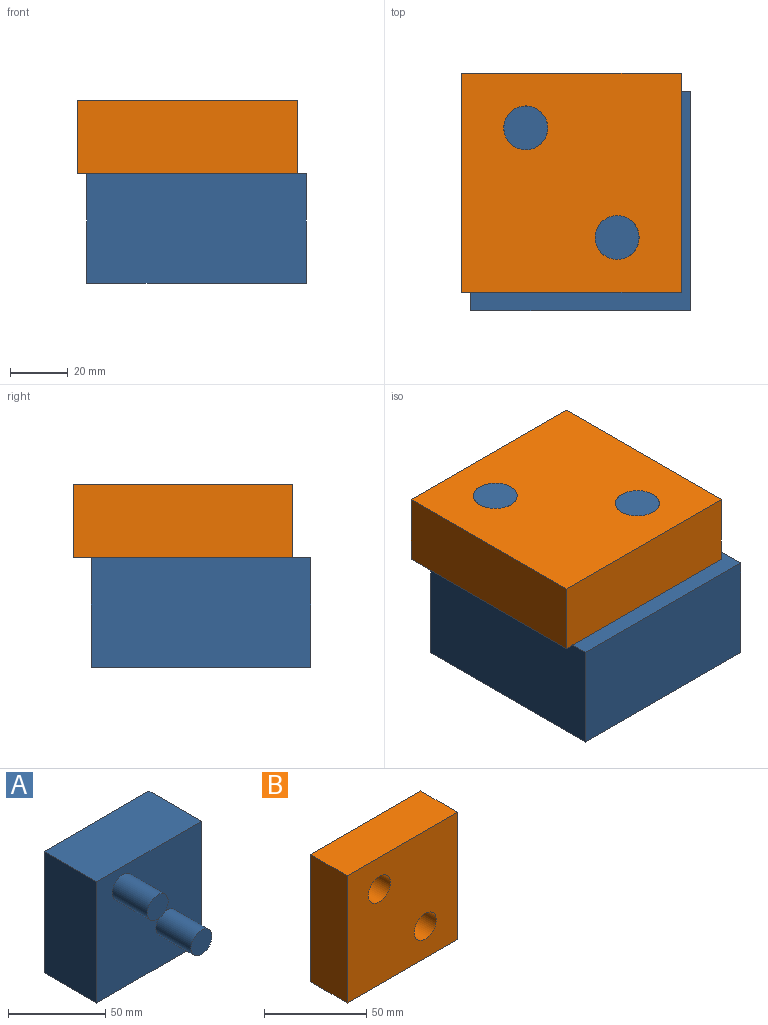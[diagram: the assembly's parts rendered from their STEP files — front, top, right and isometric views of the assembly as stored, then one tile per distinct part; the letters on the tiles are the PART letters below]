
ASSEMBLY  parts=2 mates=1
PART A: 10 faces, bbox 76.2x63.5x76.2 mm
  f0: plane 76.2x38.1mm, normal (1,0,0), area 2903.2mm2, adj f1,f3,f4,f5
  f1: plane 76.2x38.1mm, normal (0,0,1), area 2903.2mm2, adj f0,f2,f4,f5
  f2: plane 76.2x38.1mm, normal (-1,0,0), area 2903.2mm2, adj f1,f3,f4,f5
  f3: plane 76.2x38.1mm, normal (0,0,-1), area 2903.2mm2, adj f0,f2,f4,f5
  f4: plane 76.2x76.2mm, normal (0,-1,0), area 5441.6mm2, adj f0,f1,f2,f3,f6,f8
  f5: plane 76.2x76.2mm, normal (0,1,0), area 5806.4mm2, adj f0,f1,f2,f3
  f6: cylinder r=7.62mm len=25.4mm, axis (0,1,0), area 1216.1mm2, adj f4,f7
  f7: plane 15.24x15.24mm, normal (0,-1,0), area 182.4mm2, adj f6
  f8: cylinder r=7.62mm len=25.4mm, axis (0,1,0), area 1216.1mm2, adj f4,f9
  f9: plane 15.24x15.24mm, normal (0,-1,0), area 182.4mm2, adj f8
PART B: 8 faces, bbox 76.2x25.4x76.2 mm
  f0: plane 76.2x25.4mm, normal (1,0,0), area 1935.5mm2, adj f1,f3,f4,f5
  f1: plane 76.2x25.4mm, normal (0,0,1), area 1935.5mm2, adj f0,f2,f4,f5
  f2: plane 76.2x25.4mm, normal (-1,0,0), area 1935.5mm2, adj f1,f3,f4,f5
  f3: plane 76.2x25.4mm, normal (0,0,-1), area 1935.5mm2, adj f0,f2,f4,f5
  f4: plane 76.2x76.2mm, normal (0,-1,0), area 5441.6mm2, adj f0,f1,f2,f3,f6,f7
  f5: plane 76.2x76.2mm, normal (0,1,0), area 5441.6mm2, adj f0,f1,f2,f3,f6,f7
  f6: cylinder r=7.62mm len=25.4mm, axis (0,-1,0), area 1216.1mm2, adj f4,f5
  f7: cylinder r=7.62mm len=25.4mm, axis (0,-1,0), area 1216.1mm2, adj f4,f5
PLACE A rot(axis=(-1,0,0),90deg) t=(-0.21,0.43,-38.1)mm
PLACE B rot(axis=(0,-0.71,0.71),180deg) t=(-3.39,6.78,0)mm
MATE fastened B.f7 <-> A.f8  axis (0,0,-1) through (12.49,-12.27,0)mm
